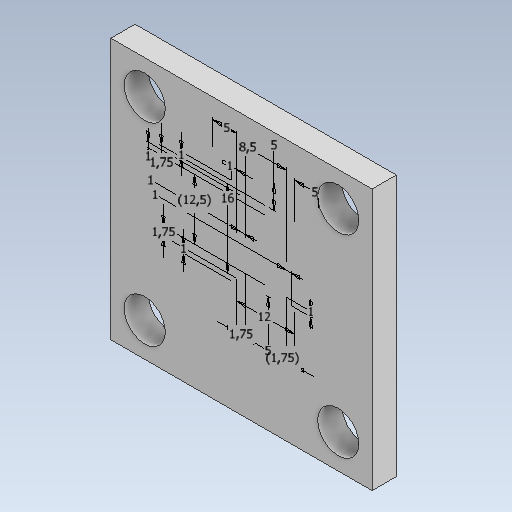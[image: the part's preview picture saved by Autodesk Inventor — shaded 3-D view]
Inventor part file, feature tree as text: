
AUTODESK INVENTOR PART (.ipt)
format: ipt  version: 2025.2 (Build 292293000, 293)  size: 327,168 bytes
history: native  units: mm
features: sketch x3, extrude x2, hole x1
ambient origin geometry x8: Origin, YZ Plane, XZ Plane, XY Plane, X Axis, Y Axis, Z Axis, Center Point
bodies: Volumenkörper1 (feature_tree)
feature tree (6):
  sketch  "Skizze1"  dims[d0=16.0mm d1=12.0mm]
  extrude  "Extrusion1"  Depth=12.0mm
  extrude  "Extrusion2"  Depth=5.0mm
  hole  "Bohrung1"  [1 undecoded]
  sketch  "Skizze2"  dims[d2=5.0mm d3=5.0mm]
  sketch  "Skizze4"  dims[d5=5.0mm d6=5.0mm d7=1.0mm d8=0.0mm d9=5.0mm d10=0.0mm d11=16.0mm d12=14.0mm d13=16.0mm d14=14.0mm d35=54.0mm d36=54.0mm d37=8.5mm d38=6.0mm d39=4.0mm d40=2.0mm d41=90.0deg d42=5.0mm d43=0.0mm d44=7.0mm d45=7.0mm d46=7.0mm d47=7.0mm d48=7.0mm d49=7.0mm d50=7.0mm d51=7.0mm d52=40.0mm d53=40.0mm d54=40.0mm d55=40.0mm d56=1.0mm d57=1.0mm d58=1.0mm d60=1.75mm d61=1.75mm d63=8.5mm d64=1.0mm d65=1.0mm d67=1.0mm d69=12.5mm d70=1.0mm d71=1.75mm d72=1.75mm]
note: 1 required parameter value undecoded (feature->parameter linkage not recoverable at this tier; creation-order binding heuristic only, values carry confidence <= 0.55)
